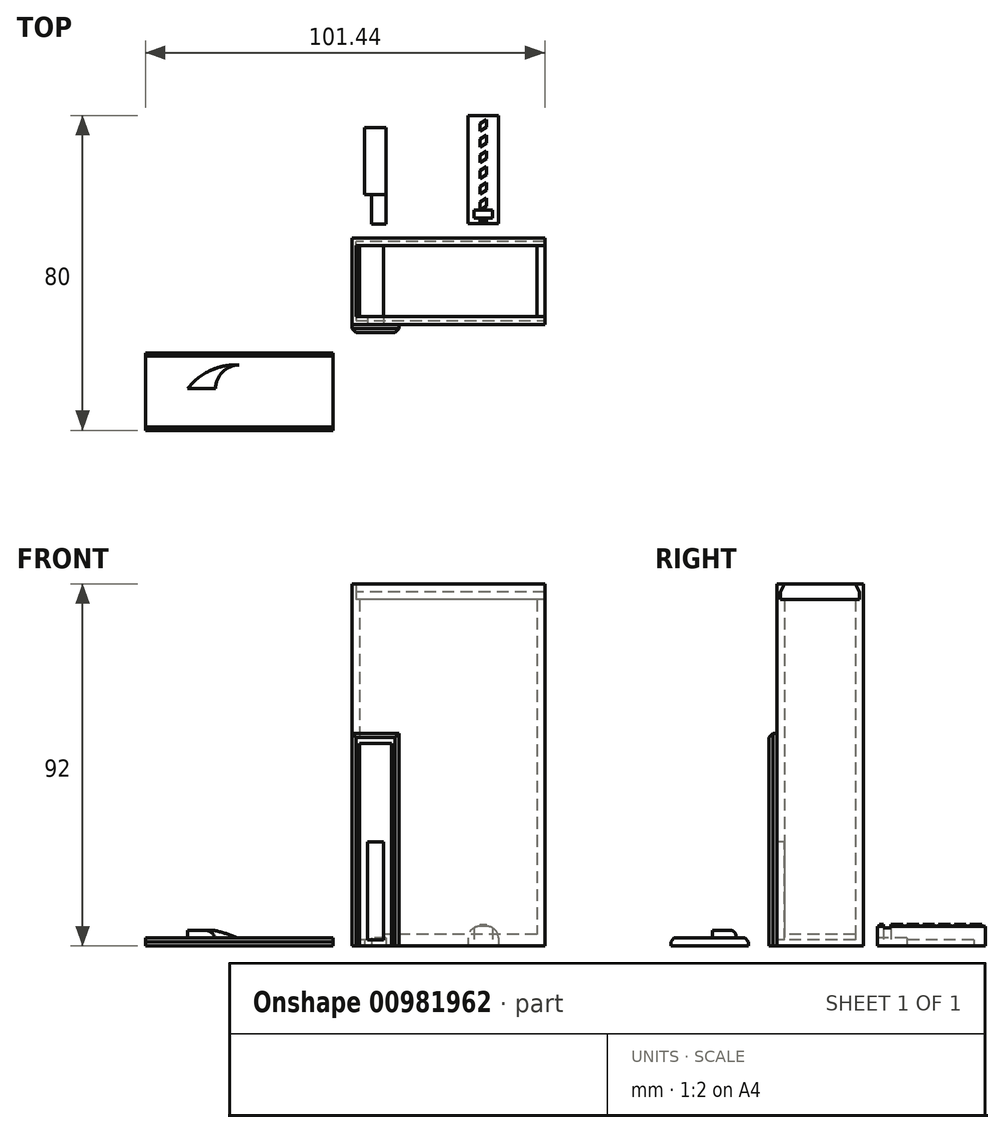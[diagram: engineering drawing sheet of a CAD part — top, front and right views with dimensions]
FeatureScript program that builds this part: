
annotation { "Feature Type Name" : "Feature", "Feature Type Description" : "" }
export const myFeature = defineFeature(function(context is Context, id is Id, definition is map)
    precondition{}
    {
        {
            var Q0;
            Q0=qCreatedBy(makeId("Top.planeOp"),FACE);
            var sketch = newSketch(context, id + "F0", { "sketchPlane" : qUnion([Q0])});
            skLineSegment(sketch, "E0.bottom", {"start": v(22.5, 9) * mm, "end": v(-22.5, 9) * mm});
            skLineSegment(sketch, "E0.top", {"start": v(22.5, -9) * mm, "end": v(-22.5, -9) * mm});
            skLineSegment(sketch, "E0.left", {"start": v(22.5, 9) * mm, "end": v(22.5, -9) * mm});
            skLineSegment(sketch, "E0.right", {"start": v(-22.5, 9) * mm, "end": v(-22.5, -9) * mm});
            skPoint(sketch, "E0.middle", {"position": v(0, 0) * mm});
            skLineSegment(sketch, "E1.bottom", {"start": v(24.5, 11) * mm, "end": v(-24.5, 11) * mm});
            skLineSegment(sketch, "E1.top", {"start": v(24.5, -11) * mm, "end": v(-24.5, -11) * mm});
            skLineSegment(sketch, "E1.left", {"start": v(24.5, 11) * mm, "end": v(24.5, -11) * mm});
            skLineSegment(sketch, "E1.right", {"start": v(-24.5, 11) * mm, "end": v(-24.5, -11) * mm});
            skSolve(sketch);
        }
        {
            var Q0;
            Q0=makeQuery(id+"F0.imprint","IMPRINT",FACE,{"disambiguationData":[TD([[makeQuery(id+"F0.imprint","IMPRINT",EDGE,{"derivedFrom":sQuery(id+"F0.wireOp",EDGE,"E0.bottom")}),-1.0]])]});
            extrude(context, id + "F1", {"entities" : qUnion([Q0]), "depth" : 88 * mm, "offsetDistance" : 25 * mm});
        }
        {
            var Q0;
            Q0=makeQuery(id+"F0.imprint","IMPRINT",FACE,{"disambiguationData":[TD([[makeQuery(id+"F0.imprint","IMPRINT",EDGE,{"derivedFrom":sQuery(id+"F0.wireOp",EDGE,"E0.bottom")}),1.0]])]});
            extrude(context, id + "F2", {"entities" : qUnion([Q0]), "operationType" : NewBodyOperationType.ADD, "depth" : 3 * mm, "offsetDistance" : 25 * mm});
        }
        {
            var Q0;
            Q0=makeQuery(id+"F1.opExtrude","SWEPT_FACE",FACE,{"disambiguationData":[OSD([sQuery(id+"F0.wireOp",EDGE,"E1.top")])]});
            var sketch = newSketch(context, id + "F3", { "sketchPlane" : qUnion([Q0])});
            skLineSegment(sketch, "E2", {"start": v(-24.5, 5.2) * mm, "end": v(-20.5, 5.2) * mm, "construction": true});
            skLineSegment(sketch, "E3", {"start": v(-20.5, 5.2) * mm, "end": v(-20.5, 0) * mm, "construction": true});
            skLineSegment(sketch, "E4", {"start": v(-20.5, 0) * mm, "end": v(-20.5, 1.5) * mm, "construction": true});
            skLineSegment(sketch, "E5", {"start": v(-20.5, 1.5) * mm, "end": v(-20.5, 26.5) * mm});
            skLineSegment(sketch, "E6", {"start": v(-20.5, 26.5) * mm, "end": v(-16.5, 26.5) * mm});
            skLineSegment(sketch, "E7", {"start": v(-16.5, 26.5) * mm, "end": v(-16.5, 1.5) * mm});
            skLineSegment(sketch, "E8", {"start": v(-16.5, 1.5) * mm, "end": v(-20.5, 1.5) * mm});
            skSolve(sketch);
        }
        {
            var Q0;
            Q0=makeQuery(id+"F3.imprint","IMPRINT",FACE,{"disambiguationData":[TD([[makeQuery(id+"F3.imprint","IMPRINT",EDGE,{"derivedFrom":sQuery(id+"F3.wireOp",EDGE,"E5")}),-1.0]])]});
            extrude(context, id + "F4", {"entities" : qUnion([Q0]), "operationType" : NewBodyOperationType.REMOVE, "oppositeDirection" : true, "depth" : 20 * mm, "offsetDistance" : 25 * mm});
        }
        {
            var Q0;
            {var subQ0=sQuery(id+"F0.wireOp",EDGE,"E0.top");var subQ2=sQuery(id+"F0.wireOp",EDGE,"E0.right");var subQ3=sQuery(id+"F0.wireOp",EDGE,"E0.bottom");Q0=makeQuery(id+"F4.boolean.opBoolean","SPLIT",FACE,{"disambiguationData":[TD([makeQuery(id+"F1.opExtrude","SWEPT_FACE",FACE,{"disambiguationData":[OSD([subQ2])]})])],"derivedFrom":makeQuery(id+"F2.opExtrude","CAP_FACE",FACE,{"disambiguationData":[OSD([subQ3,subQ0,sQuery(id+"F0.wireOp",EDGE,"E0.left"),subQ2])],"isStart":false})});}
            extrude(context, id + "F5", {"entities" : qUnion([Q0]), "operationType" : NewBodyOperationType.REMOVE, "oppositeDirection" : true, "depth" : 1.5 * mm, "offsetDistance" : 25 * mm});
        }
        {
            var Q0;
            Q0=makeQuery(id+"F1.opExtrude","SWEPT_FACE",FACE,{"disambiguationData":[OSD([sQuery(id+"F0.wireOp",EDGE,"E1.top")])]});
            var sketch = newSketch(context, id + "F6", { "sketchPlane" : qUnion([Q0])});
            skLineSegment(sketch, "E9", {"start": v(-20.5, 1.5) * mm, "end": v(-24.5, 1.5) * mm});
            skLineSegment(sketch, "E10", {"start": v(-16.5, 1.5) * mm, "end": v(-12.5, 1.5) * mm});
            skLineSegment(sketch, "E11", {"start": v(-12.5, 1.5) * mm, "end": v(-12.5, 51.5) * mm});
            skLineSegment(sketch, "E12", {"start": v(-12.5, 51.5) * mm, "end": v(-14.5, 51.5) * mm});
            skLineSegment(sketch, "E13", {"start": v(-14.5, 51.5) * mm, "end": v(-14.5, 1.5) * mm});
            skLineSegment(sketch, "E14", {"start": v(-24.5, 1.5) * mm, "end": v(-24.5, 51.5) * mm});
            skLineSegment(sketch, "E15", {"start": v(-24.5, 51.5) * mm, "end": v(-22.5, 51.5) * mm});
            skLineSegment(sketch, "E16", {"start": v(-22.5, 51.5) * mm, "end": v(-22.5, 1.5) * mm});
            skLineSegment(sketch, "E17", {"start": v(-22.5, 51.5) * mm, "end": v(-14.5, 51.5) * mm});
            skLineSegment(sketch, "E18", {"start": v(-12.5, 51.5) * mm, "end": v(-12.5, 54) * mm});
            skLineSegment(sketch, "E19", {"start": v(-12.5, 54) * mm, "end": v(-24.5, 54) * mm});
            skLineSegment(sketch, "E20", {"start": v(-22.5, 1.5) * mm, "end": v(-22.5, 0) * mm});
            skLineSegment(sketch, "E21", {"start": v(-14.5, 1.5) * mm, "end": v(-14.5, 0) * mm});
            skLineSegment(sketch, "E22", {"start": v(-14.5, 0) * mm, "end": v(-12.5, 0) * mm});
            skLineSegment(sketch, "E23", {"start": v(-12.5, 0) * mm, "end": v(-12.5, 1.5) * mm});
            skSolve(sketch);
        }
        {
            var Q0;
            {var subQ0=sQuery(id+"F6.wireOp",EDGE,"E14");Q0=makeQuery(id+"F6.imprint","IMPRINT",FACE,{"disambiguationData":[TD([[makeQuery(id+"F6.imprint","IMPRINT",EDGE,{"derivedFrom":subQ0}),1.0]])]});}
            var Q1;
            Q1=makeQuery(id+"F6.imprint","IMPRINT",FACE,{"disambiguationData":[TD([[makeQuery(id+"F6.imprint","IMPRINT",EDGE,{"derivedFrom":sQuery(id+"F6.wireOp",EDGE,"E12")}),-1.0]])]});
            var Q2;
            {var subQ0=sQuery(id+"F6.wireOp",EDGE,"E11");Q2=makeQuery(id+"F6.imprint","IMPRINT",FACE,{"disambiguationData":[TD([[makeQuery(id+"F6.imprint","IMPRINT",EDGE,{"derivedFrom":subQ0}),1.0]])]});}
            var Q3;
            {var subQ4=sQuery(id+"F6.wireOp",EDGE,"E20");Q3=makeQuery(id+"F6.imprint","IMPRINT",FACE,{"disambiguationData":[TD([[makeQuery(id+"F6.imprint","IMPRINT",EDGE,{"derivedFrom":subQ4}),-1.0]])]});}
            var Q4;
            {var subQ2=sQuery(id+"F6.wireOp",EDGE,"E21");Q4=makeQuery(id+"F6.imprint","IMPRINT",FACE,{"disambiguationData":[TD([[makeQuery(id+"F6.imprint","IMPRINT",EDGE,{"derivedFrom":subQ2}),1.0]])]});}
            extrude(context, id + "F7", {"entities" : qUnion([Q0, Q1, Q2, Q3, Q4]), "operationType" : NewBodyOperationType.ADD, "depth" : 2 * mm, "offsetDistance" : 25 * mm});
        }
        {
            var Q0;
            Q0=makeQuery(id+"F7.opExtrude","CAP_EDGE",EDGE,{"disambiguationData":[OSD([sQuery(id+"F6.wireOp",EDGE,"E19")])],"isStart":false});
            var Q1;
            Q1=makeQuery(id+"F7.opExtrude","CAP_EDGE",EDGE,{"disambiguationData":[OSD([sQuery(id+"F0.wireOp",EDGE,"E1.top"),sQuery(id+"F0.wireOp",EDGE,"E1.right"),sQuery(id+"F6.wireOp",EDGE,"E14")])],"isStart":false});
            var Q2;
            Q2=makeQuery(id+"F7.opExtrude","CAP_EDGE",EDGE,{"disambiguationData":[OSD([sQuery(id+"F6.wireOp",EDGE,"E11"),sQuery(id+"F6.wireOp",EDGE,"E18"),sQuery(id+"F6.wireOp",EDGE,"E23")])],"isStart":false});
            chamfer(context, id + "F8", {"entities" : qUnion([Q0, Q1, Q2]), "width" : 1 * mm, "tangentPropagation" : true});
        }
        {
            var Q0;
            Q0=qCreatedBy(makeId("Top.planeOp"),FACE);
            var sketch = newSketch(context, id + "F9", { "sketchPlane" : qUnion([Q0])});
            skLineSegment(sketch, "E24.bottom", {"start": v(-15.82, 39.05) * mm, "end": v(-21.32, 39.05) * mm});
            skLineSegment(sketch, "E24.top", {"start": v(-15.82, 22.05) * mm, "end": v(-21.32, 22.05) * mm});
            skLineSegment(sketch, "E24.left", {"start": v(-15.82, 39.05) * mm, "end": v(-15.82, 22.05) * mm});
            skLineSegment(sketch, "E24.right", {"start": v(-21.32, 39.05) * mm, "end": v(-21.32, 22.05) * mm});
            skPoint(sketch, "E24.middle", {"position": v(-18.57, 30.55) * mm});
            skLineSegment(sketch, "E25", {"start": v(-15.82, 22.05) * mm, "end": v(-19.52, 22.05) * mm, "construction": true});
            skLineSegment(sketch, "E26", {"start": v(-19.52, 22.05) * mm, "end": v(-19.52, 14.55) * mm});
            skLineSegment(sketch, "E27", {"start": v(-19.52, 14.55) * mm, "end": v(-15.82, 14.55) * mm});
            skLineSegment(sketch, "E28", {"start": v(-15.82, 22.05) * mm, "end": v(-15.82, 14.55) * mm});
            skLineSegment(sketch, "E29", {"start": v(-19.52, 22.05) * mm, "end": v(-19.52, 20.55) * mm, "construction": true});
            skLineSegment(sketch, "E30", {"start": v(-19.52, 20.55) * mm, "end": v(-15.82, 20.55) * mm});
            skLineSegment(sketch, "E31.bottom", {"start": v(12.7, 42.08) * mm, "end": v(5, 42.08) * mm});
            skLineSegment(sketch, "E31.top", {"start": v(12.7, 14.58) * mm, "end": v(5, 14.58) * mm});
            skLineSegment(sketch, "E31.left", {"start": v(12.7, 42.08) * mm, "end": v(12.7, 14.58) * mm});
            skLineSegment(sketch, "E31.right", {"start": v(5, 42.08) * mm, "end": v(5, 14.58) * mm});
            skPoint(sketch, "E31.middle", {"position": v(8.86, 28.33) * mm});
            skLineSegment(sketch, "E32", {"start": v(8.86, 14.58) * mm, "end": v(8.86, 16.08) * mm, "construction": true});
            skLineSegment(sketch, "E33", {"start": v(8.86, 16.08) * mm, "end": v(11.16, 16.08) * mm});
            skLineSegment(sketch, "E34", {"start": v(8.86, 16.08) * mm, "end": v(6.56, 16.08) * mm});
            skLineSegment(sketch, "E35", {"start": v(6.56, 16.08) * mm, "end": v(6.56, 18.08) * mm});
            skLineSegment(sketch, "E36", {"start": v(6.56, 18.08) * mm, "end": v(11.16, 18.08) * mm});
            skLineSegment(sketch, "E37", {"start": v(11.16, 18.08) * mm, "end": v(11.16, 16.08) * mm});
            skSolve(sketch);
        }
        {
            var Q0;
            Q0=makeQuery(id+"F9.imprint","IMPRINT",FACE,{"disambiguationData":[TD([[makeQuery(id+"F9.imprint","IMPRINT",EDGE,{"derivedFrom":sQuery(id+"F9.wireOp",EDGE,"E24.bottom")}),1.0]])]});
            extrude(context, id + "F10", {"entities" : qUnion([Q0]), "depth" : 1.5 * mm, "offsetDistance" : 25 * mm});
        }
        {
            var Q0;
            {var subQ0=sQuery(id+"F9.wireOp",EDGE,"E27");Q0=makeQuery(id+"F9.imprint","IMPRINT",FACE,{"disambiguationData":[TD([[makeQuery(id+"F9.imprint","IMPRINT",EDGE,{"derivedFrom":subQ0}),1.0]])]});}
            var Q1;
            {var subQ5=sQuery(id+"F9.wireOp",EDGE,"E30");Q1=makeQuery(id+"F9.imprint","IMPRINT",FACE,{"disambiguationData":[TD([[makeQuery(id+"F9.imprint","IMPRINT",EDGE,{"derivedFrom":subQ5}),1.0]])]});}
            extrude(context, id + "F11", {"entities" : qUnion([Q0, Q1]), "operationType" : NewBodyOperationType.ADD, "depth" : 2 * mm, "offsetDistance" : 25 * mm});
        }
        {
            var Q0;
            Q0=makeQuery(id+"F9.imprint","IMPRINT",FACE,{"disambiguationData":[TD([[makeQuery(id+"F9.imprint","IMPRINT",EDGE,{"derivedFrom":sQuery(id+"F9.wireOp",EDGE,"E31.bottom")}),1.0]])]});
            var Q1;
            Q1=makeQuery(id+"F9.imprint","IMPRINT",FACE,{"disambiguationData":[TD([[makeQuery(id+"F9.imprint","IMPRINT",EDGE,{"derivedFrom":sQuery(id+"F9.wireOp",EDGE,"E33")}),1.0]])]});
            extrude(context, id + "F12", {"entities" : qUnion([Q0, Q1]), "depth" : 5 * mm, "offsetDistance" : 25 * mm});
        }
        {
            var Q0;
            Q0=makeQuery(id+"F9.imprint","IMPRINT",FACE,{"disambiguationData":[TD([[makeQuery(id+"F9.imprint","IMPRINT",EDGE,{"derivedFrom":sQuery(id+"F9.wireOp",EDGE,"E33")}),1.0]])]});
            extrude(context, id + "F13", {"entities" : qUnion([Q0]), "operationType" : NewBodyOperationType.REMOVE, "depth" : 2.5 * mm, "offsetDistance" : 25 * mm});
        }
        {
            var Q0;
            Q0=makeQuery(id+"F12.opExtrude","CAP_EDGE",EDGE,{"disambiguationData":[OSD([sQuery(id+"F9.wireOp",EDGE,"E31.right")])],"isStart":false});
            var Q1;
            Q1=makeQuery(id+"F12.opExtrude","CAP_EDGE",EDGE,{"disambiguationData":[OSD([sQuery(id+"F9.wireOp",EDGE,"E31.left")])],"isStart":false});
            fillet(context, id + "F14", {"entities" : qUnion([Q0, Q1]), "radius" : 3 * mm, "tangentPropagation" : true, "allowEdgeOverflow" : false});
        }
        {
            var Q0;
            Q0=makeQuery(id+"F12.opExtrude","CAP_FACE",FACE,{"disambiguationData":[OSD([sQuery(id+"F9.wireOp",EDGE,"E31.bottom"),sQuery(id+"F9.wireOp",EDGE,"E31.top"),sQuery(id+"F9.wireOp",EDGE,"E31.left"),sQuery(id+"F9.wireOp",EDGE,"E31.right")])],"isStart":false});
            var sketch = newSketch(context, id + "F15", { "sketchPlane" : qUnion([Q0])});
            skLineSegment(sketch, "E38", {"start": v(8, 42.08) * mm, "end": v(8, 41.08) * mm});
            skLineSegment(sketch, "E39", {"start": v(8, 41.08) * mm, "end": v(9.7, 41.08) * mm});
            skLineSegment(sketch, "E40", {"start": v(9.7, 41.08) * mm, "end": v(9.7, 42.08) * mm});
            skLineSegment(sketch, "E41", {"start": v(9.7, 42.08) * mm, "end": v(8, 42.08) * mm});
            skLineSegment(sketch, "E42", {"start": v(8, 41.08) * mm, "end": v(8, 40.08) * mm});
            skLineSegment(sketch, "E43", {"start": v(8, 40.08) * mm, "end": v(8, 39.08) * mm});
            skLineSegment(sketch, "E44", {"start": v(8, 39.08) * mm, "end": v(8, 38.08) * mm});
            skLineSegment(sketch, "E45", {"start": v(8, 38.08) * mm, "end": v(8, 37.08) * mm});
            skLineSegment(sketch, "E46", {"start": v(8, 37.08) * mm, "end": v(8, 36.08) * mm});
            skLineSegment(sketch, "E47", {"start": v(8, 36.08) * mm, "end": v(8, 35.08) * mm});
            skLineSegment(sketch, "E48", {"start": v(8, 35.08) * mm, "end": v(8, 34.08) * mm});
            skLineSegment(sketch, "E49", {"start": v(8, 34.08) * mm, "end": v(8, 33.08) * mm});
            skLineSegment(sketch, "E50", {"start": v(8, 33.08) * mm, "end": v(8, 32.08) * mm});
            skLineSegment(sketch, "E51", {"start": v(8, 32.08) * mm, "end": v(8, 31.08) * mm});
            skLineSegment(sketch, "E52", {"start": v(8, 31.08) * mm, "end": v(8, 30.08) * mm});
            skLineSegment(sketch, "E53", {"start": v(8, 30.08) * mm, "end": v(8, 29.08) * mm});
            skLineSegment(sketch, "E54", {"start": v(8, 29.08) * mm, "end": v(8, 28.08) * mm});
            skLineSegment(sketch, "E55", {"start": v(8, 28.08) * mm, "end": v(8, 27.08) * mm});
            skLineSegment(sketch, "E56", {"start": v(8, 27.08) * mm, "end": v(8, 26.08) * mm});
            skLineSegment(sketch, "E57", {"start": v(8, 26.08) * mm, "end": v(8, 25.08) * mm});
            skLineSegment(sketch, "E58", {"start": v(8, 25.08) * mm, "end": v(8, 24.08) * mm});
            skLineSegment(sketch, "E59", {"start": v(8, 24.08) * mm, "end": v(8, 23.08) * mm});
            skLineSegment(sketch, "E60", {"start": v(8, 23.08) * mm, "end": v(8, 22.08) * mm});
            skLineSegment(sketch, "E61", {"start": v(8, 22.08) * mm, "end": v(8, 21.08) * mm});
            skLineSegment(sketch, "E62", {"start": v(8, 21.08) * mm, "end": v(8, 20.08) * mm});
            skLineSegment(sketch, "E63", {"start": v(8, 20.08) * mm, "end": v(8, 19.08) * mm});
            skLineSegment(sketch, "E64", {"start": v(8, 19.08) * mm, "end": v(8, 18.08) * mm});
            skLineSegment(sketch, "E65", {"start": v(8, 18.08) * mm, "end": v(8, 17.08) * mm});
            skLineSegment(sketch, "E66", {"start": v(8, 17.08) * mm, "end": v(8, 16.08) * mm});
            skLineSegment(sketch, "E67", {"start": v(8, 16.08) * mm, "end": v(8, 15.08) * mm});
            skLineSegment(sketch, "E68", {"start": v(8, 15.08) * mm, "end": v(9.7, 15.08) * mm});
            skLineSegment(sketch, "E69", {"start": v(9.7, 15.08) * mm, "end": v(8, 16.08) * mm});
            skLineSegment(sketch, "E70", {"start": v(8, 16.08) * mm, "end": v(9.7, 17.08) * mm});
            skLineSegment(sketch, "E71", {"start": v(9.7, 17.08) * mm, "end": v(8, 18.08) * mm});
            skLineSegment(sketch, "E72", {"start": v(8, 18.08) * mm, "end": v(9.7, 19.08) * mm});
            skLineSegment(sketch, "E73", {"start": v(9.7, 19.08) * mm, "end": v(8, 20.08) * mm});
            skLineSegment(sketch, "E74", {"start": v(8, 20.08) * mm, "end": v(9.7, 21.08) * mm});
            skLineSegment(sketch, "E75", {"start": v(9.7, 21.08) * mm, "end": v(8, 22.08) * mm});
            skLineSegment(sketch, "E76", {"start": v(8, 22.08) * mm, "end": v(9.7, 23.08) * mm});
            skLineSegment(sketch, "E77", {"start": v(9.7, 23.08) * mm, "end": v(8, 24.08) * mm});
            skLineSegment(sketch, "E78", {"start": v(8, 24.08) * mm, "end": v(9.7, 25.08) * mm});
            skLineSegment(sketch, "E79", {"start": v(9.7, 25.08) * mm, "end": v(8, 26.08) * mm});
            skLineSegment(sketch, "E80", {"start": v(8, 26.08) * mm, "end": v(9.7, 27.08) * mm});
            skLineSegment(sketch, "E81", {"start": v(9.7, 27.08) * mm, "end": v(8, 28.08) * mm});
            skLineSegment(sketch, "E82", {"start": v(8, 28.08) * mm, "end": v(9.7, 29.08) * mm});
            skLineSegment(sketch, "E83", {"start": v(9.7, 29.08) * mm, "end": v(8, 30.08) * mm});
            skLineSegment(sketch, "E84", {"start": v(8, 30.08) * mm, "end": v(9.7, 31.08) * mm});
            skLineSegment(sketch, "E85", {"start": v(9.7, 31.08) * mm, "end": v(8, 32.08) * mm});
            skLineSegment(sketch, "E86", {"start": v(8, 32.08) * mm, "end": v(9.7, 33.08) * mm});
            skLineSegment(sketch, "E87", {"start": v(9.7, 33.08) * mm, "end": v(8, 34.08) * mm});
            skLineSegment(sketch, "E88", {"start": v(8, 34.08) * mm, "end": v(9.7, 35.08) * mm});
            skLineSegment(sketch, "E89", {"start": v(9.7, 35.08) * mm, "end": v(8, 36.08) * mm});
            skLineSegment(sketch, "E90", {"start": v(8, 36.08) * mm, "end": v(9.7, 37.08) * mm});
            skLineSegment(sketch, "E91", {"start": v(9.7, 37.08) * mm, "end": v(8, 38.08) * mm});
            skLineSegment(sketch, "E92", {"start": v(8, 38.08) * mm, "end": v(9.7, 39.08) * mm});
            skLineSegment(sketch, "E93", {"start": v(9.7, 39.08) * mm, "end": v(8, 40.08) * mm});
            skLineSegment(sketch, "E94", {"start": v(8, 40.08) * mm, "end": v(9.7, 41.08) * mm});
            skSolve(sketch);
        }
        {
            var Q0;
            {var subQ0=sQuery(id+"F15.wireOp",EDGE,"E93");Q0=makeQuery(id+"F15.imprint","IMPRINT",FACE,{"disambiguationData":[TD([[makeQuery(id+"F15.imprint","IMPRINT",EDGE,{"derivedFrom":subQ0}),-1.0]])]});}
            var Q1;
            Q1=makeQuery(id+"F15.imprint","IMPRINT",FACE,{"disambiguationData":[TD([[makeQuery(id+"F15.imprint","IMPRINT",EDGE,{"derivedFrom":sQuery(id+"F15.wireOp",EDGE,"E43")}),1.0]])]});
            var Q2;
            {var subQ0=sQuery(id+"F15.wireOp",EDGE,"E89");Q2=makeQuery(id+"F15.imprint","IMPRINT",FACE,{"disambiguationData":[TD([[makeQuery(id+"F15.imprint","IMPRINT",EDGE,{"derivedFrom":subQ0}),-1.0]])]});}
            var Q3;
            Q3=makeQuery(id+"F15.imprint","IMPRINT",FACE,{"disambiguationData":[TD([[makeQuery(id+"F15.imprint","IMPRINT",EDGE,{"derivedFrom":sQuery(id+"F15.wireOp",EDGE,"E47")}),1.0]])]});
            var Q4;
            {var subQ0=sQuery(id+"F15.wireOp",EDGE,"E85");Q4=makeQuery(id+"F15.imprint","IMPRINT",FACE,{"disambiguationData":[TD([[makeQuery(id+"F15.imprint","IMPRINT",EDGE,{"derivedFrom":subQ0}),-1.0]])]});}
            var Q5;
            Q5=makeQuery(id+"F15.imprint","IMPRINT",FACE,{"disambiguationData":[TD([[makeQuery(id+"F15.imprint","IMPRINT",EDGE,{"derivedFrom":sQuery(id+"F15.wireOp",EDGE,"E51")}),1.0]])]});
            var Q6;
            {var subQ0=sQuery(id+"F15.wireOp",EDGE,"E81");Q6=makeQuery(id+"F15.imprint","IMPRINT",FACE,{"disambiguationData":[TD([[makeQuery(id+"F15.imprint","IMPRINT",EDGE,{"derivedFrom":subQ0}),-1.0]])]});}
            var Q7;
            Q7=makeQuery(id+"F15.imprint","IMPRINT",FACE,{"disambiguationData":[TD([[makeQuery(id+"F15.imprint","IMPRINT",EDGE,{"derivedFrom":sQuery(id+"F15.wireOp",EDGE,"E55")}),1.0]])]});
            var Q8;
            {var subQ0=sQuery(id+"F15.wireOp",EDGE,"E77");Q8=makeQuery(id+"F15.imprint","IMPRINT",FACE,{"disambiguationData":[TD([[makeQuery(id+"F15.imprint","IMPRINT",EDGE,{"derivedFrom":subQ0}),-1.0]])]});}
            var Q9;
            Q9=makeQuery(id+"F15.imprint","IMPRINT",FACE,{"disambiguationData":[TD([[makeQuery(id+"F15.imprint","IMPRINT",EDGE,{"derivedFrom":sQuery(id+"F15.wireOp",EDGE,"E59")}),1.0]])]});
            var Q10;
            {var subQ0=sQuery(id+"F15.wireOp",EDGE,"E73");Q10=makeQuery(id+"F15.imprint","IMPRINT",FACE,{"disambiguationData":[TD([[makeQuery(id+"F15.imprint","IMPRINT",EDGE,{"derivedFrom":subQ0}),-1.0]])]});}
            var Q11;
            Q11=makeQuery(id+"F15.imprint","IMPRINT",FACE,{"disambiguationData":[TD([[makeQuery(id+"F15.imprint","IMPRINT",EDGE,{"derivedFrom":sQuery(id+"F15.wireOp",EDGE,"E63")}),1.0]])]});
            var Q12;
            {var subQ0=sQuery(id+"F15.wireOp",EDGE,"E69");Q12=makeQuery(id+"F15.imprint","IMPRINT",FACE,{"disambiguationData":[TD([[makeQuery(id+"F15.imprint","IMPRINT",EDGE,{"derivedFrom":subQ0}),-1.0]])]});}
            var Q13;
            Q13=makeQuery(id+"F15.imprint","IMPRINT",FACE,{"disambiguationData":[TD([[makeQuery(id+"F15.imprint","IMPRINT",EDGE,{"derivedFrom":sQuery(id+"F15.wireOp",EDGE,"E67")}),1.0]])]});
            extrude(context, id + "F16", {"entities" : qUnion([Q0, Q1, Q2, Q3, Q4, Q5, Q6, Q7, Q8, Q9, Q10, Q11, Q12, Q13]), "operationType" : NewBodyOperationType.ADD, "depth" : 0.5 * mm, "offsetDistance" : 25 * mm});
        }
        {
            var Q0;
            Q0=makeQuery(id+"F1.opExtrude","CAP_FACE",FACE,{"disambiguationData":[OSD([sQuery(id+"F0.wireOp",EDGE,"E0.bottom"),sQuery(id+"F0.wireOp",EDGE,"E0.top"),sQuery(id+"F0.wireOp",EDGE,"E0.left"),sQuery(id+"F0.wireOp",EDGE,"E0.right"),sQuery(id+"F0.wireOp",EDGE,"E1.bottom"),sQuery(id+"F0.wireOp",EDGE,"E1.top"),sQuery(id+"F0.wireOp",EDGE,"E1.left"),sQuery(id+"F0.wireOp",EDGE,"E1.right")])],"isStart":false});
            var sketch = newSketch(context, id + "F17", { "sketchPlane" : qUnion([Q0])});
            skLineSegment(sketch, "E95", {"start": v(-22.5, 9) * mm, "end": v(-22.5, 10) * mm});
            skLineSegment(sketch, "E96", {"start": v(22.5, 9) * mm, "end": v(22.5, 10) * mm});
            skLineSegment(sketch, "E97", {"start": v(22.5, 10) * mm, "end": v(-22.5, 10) * mm});
            skLineSegment(sketch, "E98", {"start": v(-22.5, 10) * mm, "end": v(-23.5, 10) * mm});
            skLineSegment(sketch, "E99", {"start": v(-22.5, -9) * mm, "end": v(-22.5, -10) * mm});
            skLineSegment(sketch, "E100", {"start": v(22.5, -9) * mm, "end": v(22.5, -10) * mm});
            skLineSegment(sketch, "E101", {"start": v(22.5, -10) * mm, "end": v(-22.5, -10) * mm});
            skLineSegment(sketch, "E102", {"start": v(-23.5, 10) * mm, "end": v(-23.5, -10) * mm});
            skLineSegment(sketch, "E103", {"start": v(-23.5, -10) * mm, "end": v(-22.5, -10) * mm});
            skLineSegment(sketch, "E104", {"start": v(22.5, -10) * mm, "end": v(24.5, -10) * mm});
            skLineSegment(sketch, "E105", {"start": v(22.5, 10) * mm, "end": v(24.5, 10) * mm});
            skSolve(sketch);
        }
        {
            var Q0;
            Q0=makeQuery(id+"F9.imprint","IMPRINT",FACE,{"disambiguationData":[TD([[makeQuery(id+"F9.imprint","IMPRINT",EDGE,{"derivedFrom":sQuery(id+"F9.wireOp",EDGE,"E33")}),1.0]])]});
            extrude(context, id + "F18", {"entities" : qUnion([Q0]), "operationType" : NewBodyOperationType.REMOVE, "depth" : 32.1 * mm, "offsetDistance" : 25 * mm});
        }
        {
            var Q0;
            Q0=makeQuery(id+"F17.imprint","IMPRINT",FACE,{"disambiguationData":[TD([[makeQuery(id+"F17.imprint","IMPRINT",EDGE,{"derivedFrom":sQuery(id+"F17.wireOp",EDGE,"E97")}),-1.0]])]});
            extrude(context, id + "F19", {"entities" : qUnion([Q0]), "operationType" : NewBodyOperationType.ADD, "depth" : 4 * mm, "offsetDistance" : 25 * mm});
        }
        {
            var Q0;
            Q0=makeQuery(id+"F19.opExtrude","SWEPT_FACE",FACE,{"disambiguationData":[OSD([sQuery(id+"F17.wireOp",EDGE,"E102")])]});
            var sketch = newSketch(context, id + "F20", { "sketchPlane" : qUnion([Q0])});
            skLineSegment(sketch, "E106", {"start": v(-10, 92) * mm, "end": v(-10, 90) * mm});
            skLineSegment(sketch, "E107", {"start": v(-10, 90) * mm, "end": v(-9, 90) * mm});
            skLineSegment(sketch, "E108", {"start": v(-9, 90) * mm, "end": v(-9, 92) * mm});
            skLineSegment(sketch, "E109", {"start": v(-9, 92) * mm, "end": v(-10, 90) * mm});
            skLineSegment(sketch, "E110.MirrorCS", {"start": v(9, 92) * mm, "end": v(10, 90) * mm});
            skLineSegment(sketch, "E111.MirrorCS", {"start": v(10, 92) * mm, "end": v(10, 90) * mm});
            skLineSegment(sketch, "E112", {"start": v(-10, 92) * mm, "end": v(-9, 92) * mm});
            skLineSegment(sketch, "E113", {"start": v(9, 92) * mm, "end": v(10, 92) * mm});
            skSolve(sketch);
        }
        {
            var Q0;
            Q0=makeQuery(id+"F20.imprint","IMPRINT",FACE,{"disambiguationData":[TD([[makeQuery(id+"F20.imprint","IMPRINT",EDGE,{"derivedFrom":sQuery(id+"F20.wireOp",EDGE,"E106")}),1.0]])]});
            var Q1;
            Q1=makeQuery(id+"F20.imprint","IMPRINT",FACE,{"disambiguationData":[TD([[makeQuery(id+"F20.imprint","IMPRINT",EDGE,{"derivedFrom":sQuery(id+"F20.wireOp",EDGE,"E110.MirrorCS")}),1.0]])]});
            extrude(context, id + "F21", {"entities" : qUnion([Q0, Q1]), "operationType" : NewBodyOperationType.ADD, "depth" : 48 * mm, "offsetDistance" : 25 * mm});
        }
        {
            var Q0;
            Q0=qCreatedBy(makeId("Top.planeOp"),FACE);
            var sketch = newSketch(context, id + "F22", { "sketchPlane" : qUnion([Q0])});
            skLineSegment(sketch, "E114.bottom", {"start": v(-29.34, -37.92) * mm, "end": v(-76.94, -37.92) * mm});
            skLineSegment(sketch, "E114.top", {"start": v(-29.34, -18.22) * mm, "end": v(-76.94, -18.22) * mm});
            skLineSegment(sketch, "E114.left", {"start": v(-29.34, -37.92) * mm, "end": v(-29.34, -18.22) * mm});
            skLineSegment(sketch, "E114.right", {"start": v(-76.94, -37.92) * mm, "end": v(-76.94, -18.22) * mm});
            skPoint(sketch, "E114.middle", {"position": v(-53.14, -28.07) * mm});
            skSolve(sketch);
        }
        {
            var Q0;
            Q0=makeQuery(id+"F22.imprint","IMPRINT",FACE,{"disambiguationData":[TD([[makeQuery(id+"F22.imprint","IMPRINT",EDGE,{"derivedFrom":sQuery(id+"F22.wireOp",EDGE,"E114.bottom")}),-1.0]])]});
            extrude(context, id + "F23", {"entities" : qUnion([Q0]), "depth" : 2 * mm, "offsetDistance" : 25 * mm});
        }
        {
            var Q0;
            Q0=makeQuery(id+"F23.opExtrude","SWEPT_FACE",FACE,{"disambiguationData":[OSD([sQuery(id+"F22.wireOp",EDGE,"E114.left")])]});
            var sketch = newSketch(context, id + "F24", { "sketchPlane" : qUnion([Q0])});
            skLineSegment(sketch, "E115", {"start": v(-28.07, 2) * mm, "end": v(-19.07, 2) * mm});
            skLineSegment(sketch, "E116", {"start": v(-28.07, 2) * mm, "end": v(-37.07, 2) * mm});
            skLineSegment(sketch, "E117", {"start": v(-37.92, 0) * mm, "end": v(-37.92, 1) * mm});
            skLineSegment(sketch, "E118", {"start": v(-37.92, 1) * mm, "end": v(-37.07, 2) * mm});
            skLineSegment(sketch, "E119", {"start": v(-18.22, 0) * mm, "end": v(-18.22, 1) * mm});
            skLineSegment(sketch, "E120", {"start": v(-18.22, 1) * mm, "end": v(-19.07, 2) * mm});
            skSolve(sketch);
        }
        {
            var Q0;
            {var subQ0=sQuery(id+"F24.wireOp",EDGE,"E118");Q0=makeQuery(id+"F24.imprint","IMPRINT",FACE,{"disambiguationData":[TD([[makeQuery(id+"F24.imprint","IMPRINT",EDGE,{"derivedFrom":subQ0}),1.0]])]});}
            var Q1;
            {var subQ0=sQuery(id+"F24.wireOp",EDGE,"E120");Q1=makeQuery(id+"F24.imprint","IMPRINT",FACE,{"disambiguationData":[TD([[makeQuery(id+"F24.imprint","IMPRINT",EDGE,{"derivedFrom":subQ0}),-1.0]])]});}
            extrude(context, id + "F25", {"entities" : qUnion([Q0, Q1]), "operationType" : NewBodyOperationType.REMOVE, "oppositeDirection" : true, "depth" : 49 * mm, "offsetDistance" : 25 * mm});
        }
        {
            var Q0;
            Q0=makeQuery(id+"F23.opExtrude","CAP_FACE",FACE,{"disambiguationData":[OSD([sQuery(id+"F22.wireOp",EDGE,"E114.bottom"),sQuery(id+"F22.wireOp",EDGE,"E114.top"),sQuery(id+"F22.wireOp",EDGE,"E114.left"),sQuery(id+"F22.wireOp",EDGE,"E114.right")])],"isStart":false});
            var sketch = newSketch(context, id + "F26", { "sketchPlane" : qUnion([Q0])});
            skLineSegment(sketch, "E121", {"start": v(-76.94, -27.35) * mm, "end": v(-29.34, -27.35) * mm});
            skCircle(sketch, "E122", {"center": v(-53.14, -27.35) * mm, "radius": 6.01 * mm});
            skArc(sketch, "E123", {"start": v(-52.92, -21.33) * mm, "mid": v(-53.23, -21.34) * mm, "end": v(-53.53, -21.34) * mm});
            skLineSegment(sketch, "E124", {"start": v(-53.14, -27.35) * mm, "end": v(-53.14, -21.33) * mm});
            skArc(sketch, "E125", {"start": v(-53.14, -21.33) * mm, "mid": v(-60.43, -22.7) * mm, "end": v(-66.2, -27.35) * mm});
            skArc(sketch, "E126.MirrorCS", {"start": v(-53.14, -21.33) * mm, "mid": v(-45.84, -22.7) * mm, "end": v(-40.06, -27.35) * mm});
            skArc(sketch, "E127.MirrorCS", {"start": v(-53.14, -33.36) * mm, "mid": v(-60.43, -32) * mm, "end": v(-66.2, -27.35) * mm});
            skArc(sketch, "E128.MirrorCS", {"start": v(-53.14, -33.36) * mm, "mid": v(-45.84, -32) * mm, "end": v(-40.06, -27.35) * mm});
            skSolve(sketch);
        }
        {
            var Q0;
            {var subQ3=sQuery(id+"F26.wireOp",EDGE,"E122");var subQ5=makeQuery(id+"F26.imprint","INTERSECT",VERTEX,{"disambiguationData":[OD(1.0)],"derivedFrom":[subQ3,sQuery(id+"F26.wireOp",EDGE,"E123")]});Q0=makeQuery(id+"F26.imprint","IMPRINT",FACE,{"disambiguationData":[TD([[makeQuery(id+"F26.imprint","IMPRINT",EDGE,{"disambiguationData":[TD([[subQ5,1.0]])],"derivedFrom":subQ3}),-1.0]])]});}
            var Q1;
            {var subQ1=sQuery(id+"F26.wireOp",EDGE,"E121");var subQ3=sQuery(id+"F26.wireOp",EDGE,"E122");var subQ4=makeQuery(id+"F26.imprint","INTERSECT",VERTEX,{"disambiguationData":[OD(1.0)],"derivedFrom":[subQ1,subQ3]});Q1=makeQuery(id+"F26.imprint","IMPRINT",FACE,{"disambiguationData":[TD([[makeQuery(id+"F26.imprint","IMPRINT",EDGE,{"disambiguationData":[TD([[subQ4,1.0]])],"derivedFrom":subQ3}),-1.0]])]});}
            extrude(context, id + "F27", {"entities" : qUnion([Q0, Q1]), "operationType" : NewBodyOperationType.ADD, "depth" : 2 * mm, "offsetDistance" : 25 * mm});
        }
        {
            var Q0;
            {var subQ0=sQuery(id+"F26.wireOp",EDGE,"E122");var subQ1=makeQuery(id+"F26.imprint","INTERSECT",VERTEX,{"disambiguationData":[OD(1.0)],"derivedFrom":[subQ0,sQuery(id+"F26.wireOp",EDGE,"E123")]});Q0=makeQuery(id+"F27.opExtrude","CAP_EDGE",EDGE,{"disambiguationData":[OSD([subQ0]),TDD([makeQuery(id+"F26.imprint","IMPRINT",EDGE,{"disambiguationData":[TD([[subQ1,1.0]])],"derivedFrom":subQ0}),makeQuery(id+"F26.imprint","IMPRINT",EDGE,{"disambiguationData":[TD([[subQ1,-1.0]])],"derivedFrom":subQ0})])],"isStart":false});}
            var Q1;
            {var subQ0=sQuery(id+"F26.wireOp",EDGE,"E122");Q1=makeQuery(id+"F27.opExtrude","CAP_EDGE",EDGE,{"disambiguationData":[OSD([subQ0]),TDD([makeQuery(id+"F26.imprint","IMPRINT",EDGE,{"disambiguationData":[TD([[makeQuery(id+"F26.imprint","INTERSECT",VERTEX,{"disambiguationData":[OD(1.0)],"derivedFrom":[sQuery(id+"F26.wireOp",EDGE,"E121"),subQ0]}),1.0]])],"derivedFrom":subQ0})])],"isStart":false});}
            fillet(context, id + "F28", {"entities" : qUnion([Q0, Q1]), "radius" : 3 * mm, "tangentPropagation" : true, "allowEdgeOverflow" : false});
        }
    });
